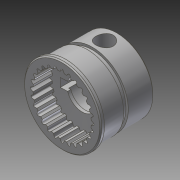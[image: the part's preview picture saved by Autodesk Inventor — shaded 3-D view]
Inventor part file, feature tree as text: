
AUTODESK INVENTOR PART (.ipt)
format: ipt  version: 2014 SP1 (Build 180222100, 222)  size: 450,560 bytes
history: native  units: in
note: dims shown in document units (in); Inventor stores cm internally (conversion verified against a paired STEP export)
features: fillet x1, other x1, imported_body x1
ambient origin geometry x8: Origin, YZ Plane, XZ Plane, XY Plane, X Axis, Y Axis, Z Axis, Center Point
bodies: Body1 (feature_tree)
feature tree (3):
  fillet  "Fillet1"  [1 undecoded]
  other  "217-2625-009 Rev1.ipt1"
  imported_body  "Base1"
note: 1 required parameter value undecoded (feature->parameter linkage not recoverable at this tier; creation-order binding heuristic only, values carry confidence <= 0.55)
